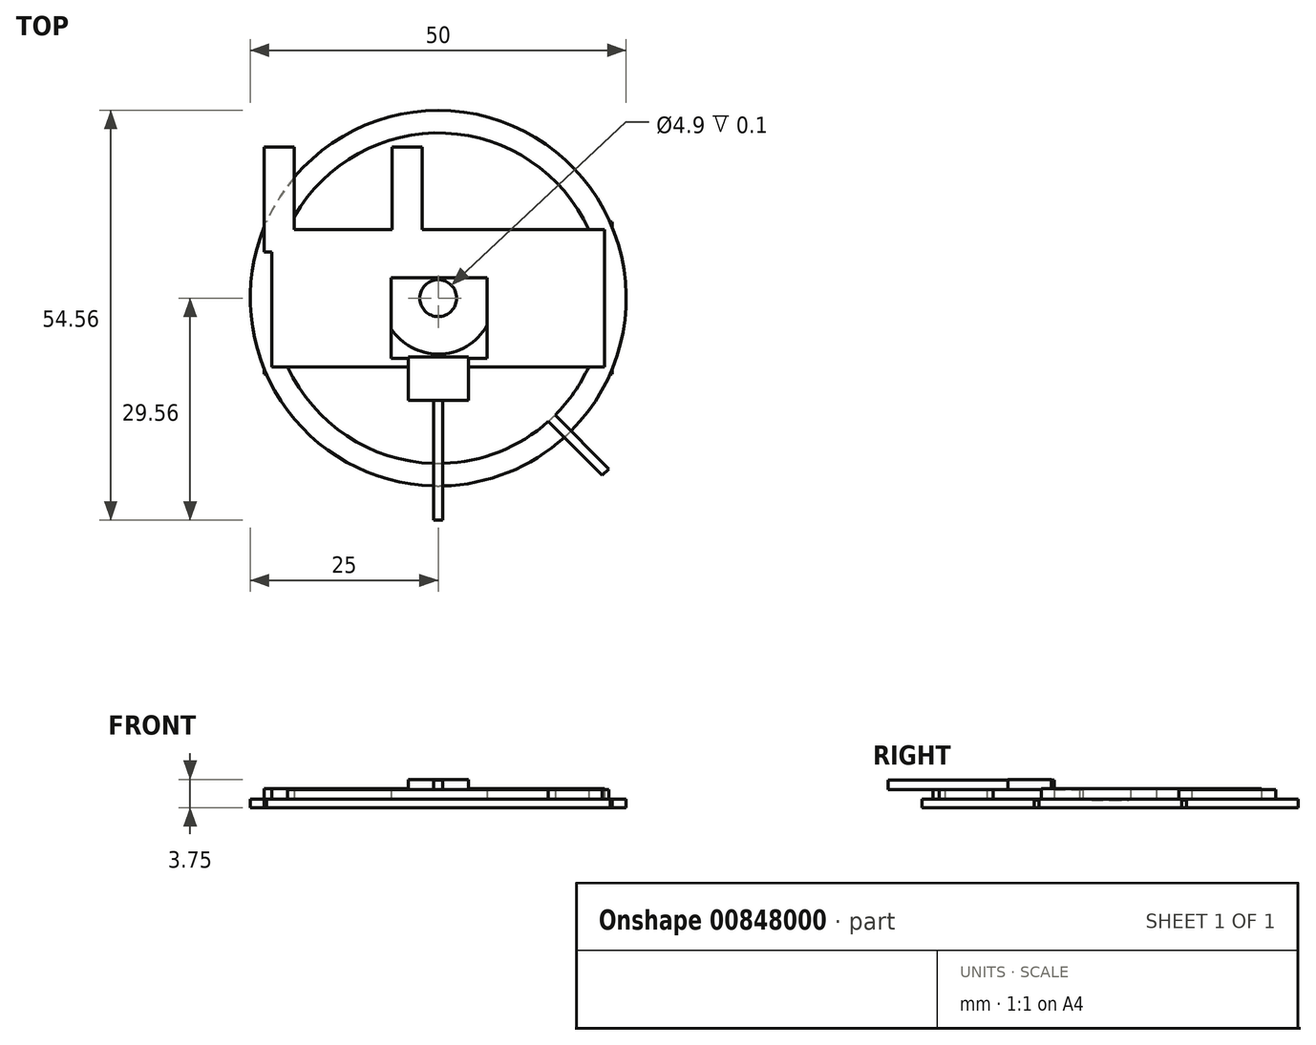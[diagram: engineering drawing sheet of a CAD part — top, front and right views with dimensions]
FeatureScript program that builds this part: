
annotation { "Feature Type Name" : "Feature", "Feature Type Description" : "" }
export const myFeature = defineFeature(function(context is Context, id is Id, definition is map)
    precondition{}
    {
        {
            var Q0;
            Q0=qCreatedBy(makeId("Top.planeOp"),FACE);
            var sketch = newSketch(context, id + "F0", { "sketchPlane" : qUnion([Q0])});
            skLineSegment(sketch, "E0.bottom", {"start": v(-23.12, 10.12) * mm, "end": v(23.12, 10.12) * mm});
            skLineSegment(sketch, "E0.top", {"start": v(-23.12, -10.12) * mm, "end": v(-6, -10.12) * mm});
            skLineSegment(sketch, "E0.left", {"start": v(-23.12, 10.12) * mm, "end": v(-23.12, -10.12) * mm});
            skLineSegment(sketch, "E0.right", {"start": v(23.12, 10.12) * mm, "end": v(23.12, -10.13) * mm});
            skCircle(sketch, "E1", {"center": v(4.63, 0.88) * mm, "radius": 0.87 * mm});
            skCircle(sketch, "E2", {"center": v(-4.38, -6.12) * mm, "radius": 0.87 * mm});
            skLineSegment(sketch, "E3.top", {"start": v(-6, -12.12) * mm, "end": v(6, -12.12) * mm});
            skLineSegment(sketch, "E3.left", {"start": v(-6, -10.12) * mm, "end": v(-6, -12.12) * mm});
            skLineSegment(sketch, "E3.right", {"start": v(6, -10.12) * mm, "end": v(6, -12.12) * mm});
            skLineSegment(sketch, "E4.trimOffspring", {"start": v(6, -10.12) * mm, "end": v(23.12, -10.12) * mm});
            skSolve(sketch);
        }
        {
            var Q0;
            Q0=makeQuery(id+"F0.imprint","IMPRINT",FACE,{"disambiguationData":[TD([[makeQuery(id+"F0.imprint","IMPRINT",EDGE,{"derivedFrom":sQuery(id+"F0.wireOp",EDGE,"E0.bottom")}),-1.0]])]});
            extrude(context, id + "F1", {"entities" : qUnion([Q0]), "depth" : 1 * mm, "offsetDistance" : 25 * mm});
        }
        {
            var Q0;
            Q0=makeQuery(id+"F1.opExtrude","CAP_FACE",FACE,{"disambiguationData":[OSD([sQuery(id+"F0.wireOp",EDGE,"E0.bottom"),sQuery(id+"F0.wireOp",EDGE,"E0.top"),sQuery(id+"F0.wireOp",EDGE,"E0.left"),sQuery(id+"F0.wireOp",EDGE,"E0.right"),sQuery(id+"F0.wireOp",EDGE,"E1"),sQuery(id+"F0.wireOp",EDGE,"E2"),sQuery(id+"F0.wireOp",EDGE,"E3.top"),sQuery(id+"F0.wireOp",EDGE,"E3.left"),sQuery(id+"F0.wireOp",EDGE,"E3.right"),sQuery(id+"F0.wireOp",EDGE,"E4.trimOffspring")])],"isStart":false});
            var sketch = newSketch(context, id + "F2", { "sketchPlane" : qUnion([Q0])});
            skLineSegment(sketch, "E5.bottom", {"start": v(-19.12, 9.13) * mm, "end": v(-6.12, 9.13) * mm});
            skLineSegment(sketch, "E5.top", {"start": v(-22.12, -9.13) * mm, "end": v(22.12, -9.13) * mm});
            skLineSegment(sketch, "E5.left", {"start": v(-22.12, 6.13) * mm, "end": v(-22.12, -9.13) * mm});
            skLineSegment(sketch, "E5.right", {"start": v(22.12, 9.13) * mm, "end": v(22.12, -9.13) * mm});
            skLineSegment(sketch, "E6.bottom", {"start": v(-6.25, 2.75) * mm, "end": v(6.5, 2.75) * mm});
            skLineSegment(sketch, "E6.top", {"start": v(-6.25, -8) * mm, "end": v(6.5, -8) * mm});
            skLineSegment(sketch, "E6.left", {"start": v(-6.25, 2.75) * mm, "end": v(-6.25, -8) * mm});
            skLineSegment(sketch, "E6.right", {"start": v(6.5, 2.75) * mm, "end": v(6.5, -8) * mm});
            skLineSegment(sketch, "E7.bottom", {"start": v(-23.12, 10.12) * mm, "end": v(-19.12, 10.12) * mm});
            skLineSegment(sketch, "E7.top", {"start": v(-23.12, 6.13) * mm, "end": v(-22.12, 6.13) * mm});
            skLineSegment(sketch, "E7.left", {"start": v(-23.12, 10.12) * mm, "end": v(-23.12, 6.13) * mm});
            skLineSegment(sketch, "E7.right", {"start": v(-19.12, 10.12) * mm, "end": v(-19.12, 9.13) * mm});
            skLineSegment(sketch, "E8.bottom", {"start": v(-6.12, 10.12) * mm, "end": v(-2.12, 10.12) * mm});
            skLineSegment(sketch, "E8.left", {"start": v(-6.12, 10.12) * mm, "end": v(-6.12, 9.13) * mm});
            skLineSegment(sketch, "E8.right", {"start": v(-2.12, 10.12) * mm, "end": v(-2.12, 9.13) * mm});
            skLineSegment(sketch, "E9.trimOffspring", {"start": v(-2.12, 9.13) * mm, "end": v(22.12, 9.13) * mm});
            skSolve(sketch);
        }
        {
            var Q0;
            Q0=makeQuery(id+"F2.imprint","IMPRINT",FACE,{"disambiguationData":[TD([[makeQuery(id+"F2.imprint","IMPRINT",EDGE,{"derivedFrom":sQuery(id+"F2.wireOp",EDGE,"E5.bottom")}),-1.0]])]});
            extrude(context, id + "F3", {"entities" : qUnion([Q0]), "operationType" : NewBodyOperationType.ADD, "depth" : 1.5 * mm, "offsetDistance" : 25 * mm});
        }
        {
            var Q0;
            {var subQ0=sQuery(id+"F0.wireOp",EDGE,"E3.right");var subQ1=sQuery(id+"F0.wireOp",EDGE,"E3.left");var subQ2=sQuery(id+"F0.wireOp",EDGE,"E3.top");var subQ3=sQuery(id+"F0.wireOp",EDGE,"E4.trimOffspring");var subQ4=sQuery(id+"F0.wireOp",EDGE,"E0.bottom");var subQ5=sQuery(id+"F0.wireOp",EDGE,"E0.right");var subQ6=sQuery(id+"F0.wireOp",EDGE,"E0.top");var subQ7=sQuery(id+"F0.wireOp",EDGE,"E0.left");Q0=makeQuery(id+"F3.boolean.opBoolean","SPLIT",FACE,{"disambiguationData":[TD([makeQuery(id+"F1.opExtrude","SWEPT_FACE",FACE,{"disambiguationData":[OSD([subQ6])]})])],"derivedFrom":makeQuery(id+"F1.opExtrude","CAP_FACE",FACE,{"disambiguationData":[OSD([subQ4,subQ6,subQ7,subQ5,sQuery(id+"F0.wireOp",EDGE,"E1"),sQuery(id+"F0.wireOp",EDGE,"E2"),subQ2,subQ1,subQ0,subQ3])],"isStart":false})});}
            var sketch = newSketch(context, id + "F4", { "sketchPlane" : qUnion([Q0])});
            skLineSegment(sketch, "E10.bottom", {"start": v(-4, -7.82) * mm, "end": v(4, -7.82) * mm});
            skLineSegment(sketch, "E10.top", {"start": v(-4, -13.62) * mm, "end": v(4, -13.62) * mm});
            skLineSegment(sketch, "E10.left", {"start": v(-4, -7.82) * mm, "end": v(-4, -13.62) * mm});
            skLineSegment(sketch, "E10.right", {"start": v(4, -7.82) * mm, "end": v(4, -13.62) * mm});
            skSolve(sketch);
        }
        {
            var Q0;
            Q0 = qSketchRegion(id + "F4", true);
            extrude(context, id + "F5", {"entities" : qUnion([Q0]), "operationType" : NewBodyOperationType.ADD, "depth" : 2.75 * mm, "offsetDistance" : 25 * mm});
        }
        {
            var Q0;
            Q0=makeQuery(id+"F3.boolean.opBoolean","MERGE",FACE,{"derivedFrom":[makeQuery(id+"F1.opExtrude","SWEPT_FACE",FACE,{"disambiguationData":[OSD([sQuery(id+"F0.wireOp",EDGE,"E0.bottom")])]}),makeQuery(id+"F3.opExtrude","SWEPT_FACE",FACE,{"disambiguationData":[OSD([sQuery(id+"F2.wireOp",EDGE,"E7.bottom")])]}),makeQuery(id+"F3.opExtrude","SWEPT_FACE",FACE,{"disambiguationData":[OSD([sQuery(id+"F2.wireOp",EDGE,"E8.bottom")])]})]});
            var sketch = newSketch(context, id + "F6", { "sketchPlane" : qUnion([Q0])});
            skLineSegment(sketch, "E11.bottom", {"start": v(2.12, 2.5) * mm, "end": v(6.12, 2.5) * mm});
            skLineSegment(sketch, "E11.top", {"start": v(2.12, 1) * mm, "end": v(6.12, 1) * mm});
            skLineSegment(sketch, "E11.left", {"start": v(2.12, 2.5) * mm, "end": v(2.12, 1) * mm});
            skLineSegment(sketch, "E11.right", {"start": v(6.12, 2.5) * mm, "end": v(6.12, 1) * mm});
            skLineSegment(sketch, "E12.bottom", {"start": v(19.12, 2.5) * mm, "end": v(23.12, 2.5) * mm});
            skLineSegment(sketch, "E12.top", {"start": v(19.12, 1) * mm, "end": v(23.12, 1) * mm});
            skLineSegment(sketch, "E12.left", {"start": v(19.12, 2.5) * mm, "end": v(19.12, 1) * mm});
            skLineSegment(sketch, "E12.right", {"start": v(23.12, 2.5) * mm, "end": v(23.12, 1) * mm});
            skSolve(sketch);
        }
        {
            var Q0;
            Q0 = qSketchRegion(id + "F6", true);
            extrude(context, id + "F7", {"entities" : qUnion([Q0]), "operationType" : NewBodyOperationType.ADD, "depth" : 10 * mm, "offsetDistance" : 25 * mm});
        }
        {
            var Q0;
            Q0=qCreatedBy(makeId("Top.planeOp"),FACE);
            var sketch = newSketch(context, id + "F8", { "sketchPlane" : qUnion([Q0])});
            skCircle(sketch, "E13", {"center": v(0, 0) * mm, "radius": 25 * mm});
            skCircle(sketch, "E14", {"center": v(0, 0) * mm, "radius": 2.45 * mm});
            skSolve(sketch);
        }
        {
            var Q0;
            Q0=makeQuery(id+"F8.imprint","IMPRINT",FACE,{"disambiguationData":[TD([[makeQuery(id+"F8.imprint","IMPRINT",EDGE,{"derivedFrom":sQuery(id+"F8.wireOp",EDGE,"E13")}),1.0]])]});
            extrude(context, id + "F9", {"entities" : qUnion([Q0]), "depth" : 1.1 * mm, "offsetDistance" : 25 * mm});
        }
        {
            var Q0;
            Q0=makeQuery(id+"F9.opExtrude","CAP_FACE",FACE,{"disambiguationData":[OSD([sQuery(id+"F8.wireOp",EDGE,"E13"),sQuery(id+"F8.wireOp",EDGE,"E14")])],"isStart":false});
            var sketch = newSketch(context, id + "F10", { "sketchPlane" : qUnion([Q0])});
            skCircle(sketch, "E15", {"center": v(0, 0) * mm, "radius": 22 * mm});
            skCircle(sketch, "E16", {"center": v(0, 0) * mm, "radius": 7.45 * mm});
            skSolve(sketch);
        }
        {
            var Q0;
            Q0=makeQuery(id+"F10.imprint","IMPRINT",FACE,{"disambiguationData":[TD([[makeQuery(id+"F10.imprint","IMPRINT",EDGE,{"derivedFrom":sQuery(id+"F10.wireOp",EDGE,"E15")}),1.0]])]});
            extrude(context, id + "F11", {"entities" : qUnion([Q0]), "operationType" : NewBodyOperationType.ADD, "depth" : 1.3 * mm, "offsetDistance" : 25 * mm});
        }
        {
            var Q0;
            Q0=makeQuery(id+"F11.opExtrude","CAP_FACE",FACE,{"disambiguationData":[OSD([sQuery(id+"F10.wireOp",EDGE,"E15"),sQuery(id+"F10.wireOp",EDGE,"E16")])],"isStart":false});
            var sketch = newSketch(context, id + "F12", { "sketchPlane" : qUnion([Q0])});
            skLineSegment(sketch, "E17.bottom", {"start": v(-0.63, -7.45) * mm, "end": v(0.63, -7.45) * mm});
            skLineSegment(sketch, "E17.top", {"start": v(-0.63, -29.56) * mm, "end": v(0.63, -29.56) * mm});
            skLineSegment(sketch, "E17.left", {"start": v(-0.63, -7.45) * mm, "end": v(-0.63, -29.56) * mm});
            skLineSegment(sketch, "E17.right", {"start": v(0.62, -7.45) * mm, "end": v(0.62, -29.56) * mm});
            skLineSegment(sketch, "E18", {"start": v(13.97, -15.73) * mm, "end": v(14.85, -14.85) * mm});
            skLineSegment(sketch, "E19", {"start": v(14.85, -14.85) * mm, "end": v(22.71, -22.71) * mm});
            skLineSegment(sketch, "E20", {"start": v(22.71, -22.71) * mm, "end": v(21.83, -23.6) * mm});
            skLineSegment(sketch, "E21", {"start": v(21.83, -23.6) * mm, "end": v(13.97, -15.73) * mm});
            skSolve(sketch);
        }
        {
            var Q0;
            {var subQ0=sQuery(id+"F12.wireOp",EDGE,"E17.left");var subQ1=sQuery(id+"F12.wireOp",EDGE,"E17.bottom");var subQ2=makeQuery(id+"F12.imprint","INTERSECT",VERTEX,{"derivedFrom":[subQ1,subQ0]});Q0=makeQuery(id+"F12.imprint","IMPRINT",FACE,{"disambiguationData":[TD([[makeQuery(id+"F12.imprint","IMPRINT",EDGE,{"disambiguationData":[TD([[subQ2,-1.0]])],"derivedFrom":subQ1}),-1.0]])]});}
            var Q1;
            {var subQ0=sQuery(id+"F12.wireOp",EDGE,"E17.top");Q1=makeQuery(id+"F12.imprint","IMPRINT",FACE,{"disambiguationData":[TD([[makeQuery(id+"F12.imprint","IMPRINT",EDGE,{"derivedFrom":subQ0}),1.0]])]});}
            extrude(context, id + "F13", {"entities" : qUnion([Q0, Q1]), "operationType" : NewBodyOperationType.ADD, "depth" : 1.25 * mm, "offsetDistance" : 25 * mm});
        }
        {
            var Q0;
            Q0=makeQuery(id+"F12.imprint","IMPRINT",FACE,{"disambiguationData":[TD([[makeQuery(id+"F12.imprint","IMPRINT",EDGE,{"derivedFrom":sQuery(id+"F12.wireOp",EDGE,"E18")}),-1.0]])]});
            var Q1;
            {var subQ0=sQuery(id+"F12.wireOp",EDGE,"E20");Q1=makeQuery(id+"F12.imprint","IMPRINT",FACE,{"disambiguationData":[TD([[makeQuery(id+"F12.imprint","IMPRINT",EDGE,{"derivedFrom":subQ0}),-1.0]])]});}
            extrude(context, id + "F14", {"entities" : qUnion([Q0, Q1]), "operationType" : NewBodyOperationType.ADD, "oppositeDirection" : true, "depth" : 1.25 * mm, "offsetDistance" : 25 * mm});
        }
    });
